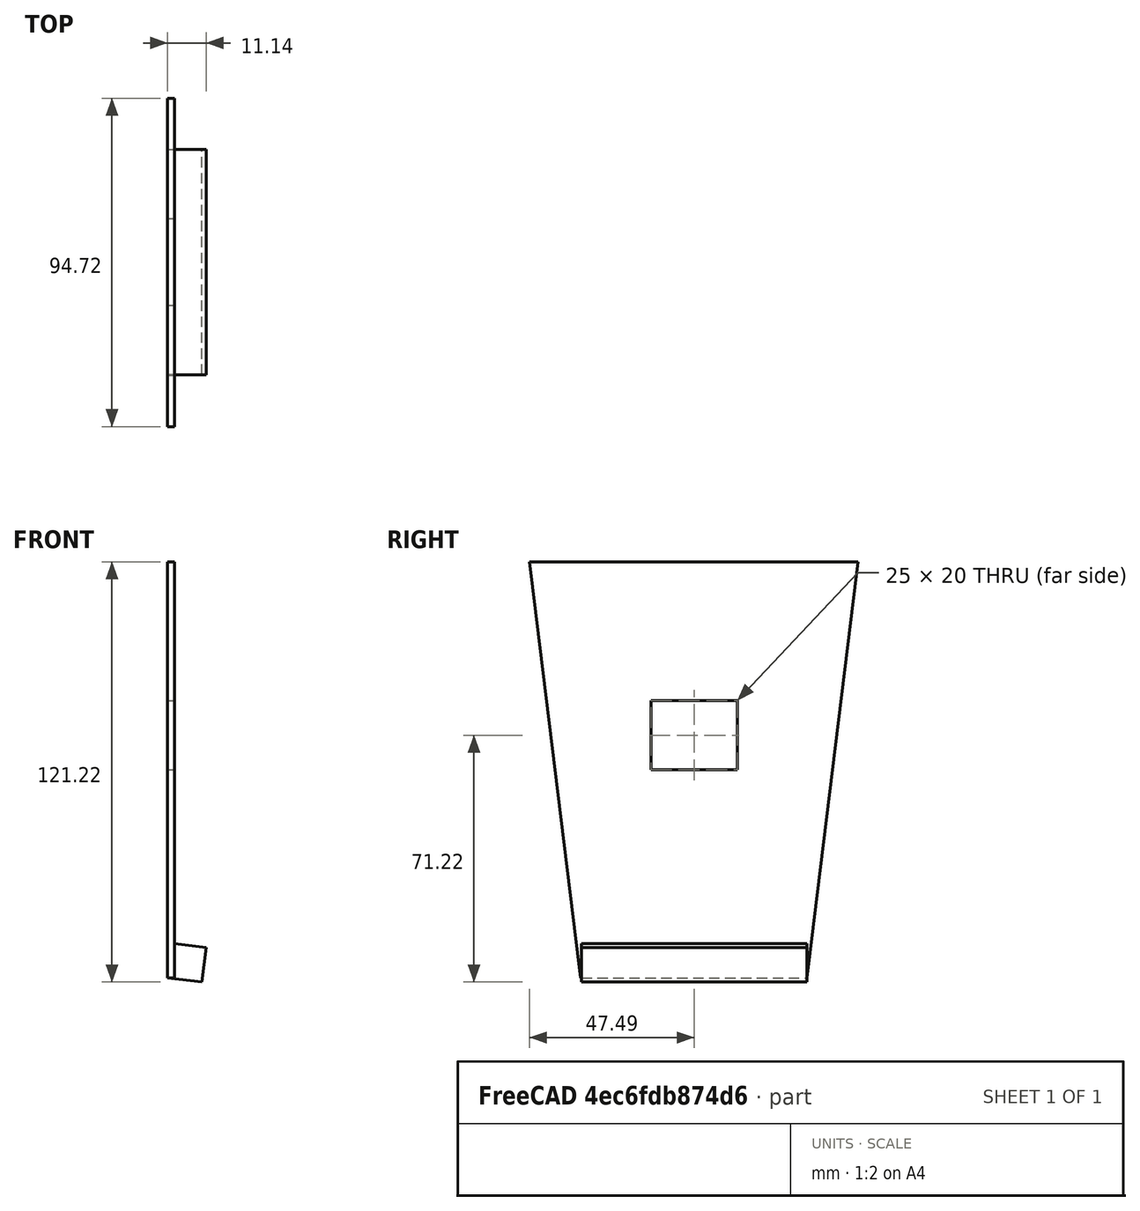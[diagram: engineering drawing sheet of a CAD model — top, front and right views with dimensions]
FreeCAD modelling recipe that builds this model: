
FCSTD DOCUMENT  (FreeCAD 0.14R3702 (Git))
Label: vertical_face_mark1
License: CC-BY 3.0
LicenseURL: http://creativecommons.org/licenses/by/3.0/
objects: Part::Box×5, Part::Cut×3, Part::MultiFuse×1
note: 9 computed .brp shape members not serialized (recipe doc carries the construction recipe); baked Part::Feature solids carry a one-line shape summary decoded from their .brp

FEATURE [Part::Box] Box  label="Cube"
  Height = 120
  Length = 2
  Width = 95
FEATURE [Part::Box] Box001  label="Cube001"
  Height = 140
  Length = 10
  Placement = pos=(0,0,-3) rot=(1,0,0;0.122173rad)
  Width = 15
FEATURE [Part::Box] Box002  label="Cube002"
  Height = 140
  Length = 10
  Placement = pos=(0,80,0) rot=(-1,0,0;0.122173rad)
  Width = 15
FEATURE [Part::Cut] Cut
  Base = -> Box
  Tool = -> Box001
FEATURE [Part::Cut] Cut001
  Base = -> Cut
  Tool = -> Box002
FEATURE [Part::Box] Box003  label="Cube003"
  Height = 20
  Length = 10
  Placement = pos=(0,35,60) rot=(0,0,1;0rad)
  Width = 25
FEATURE [Part::Cut] Cut002
  Base = -> Cut001
  Tool = -> Box003
FEATURE [Part::Box] Box004  label="Cube004"
  Height = 10
  Length = 10
  Placement = pos=(0,15,0) rot=(0,1,0;0.122173rad)
  Width = 65
FEATURE [Part::MultiFuse] Fusion
  Shapes = -> [Cut002,Box004]
